# Revit family: SupportArms_Toilet_Nero_MeccaCare_Foldable
name_source: partatom
category: Specialty Equipment
units: mm (PartAtom-declared; Revit-internal decimal feet)

## family parameters
Always vertical = Yes
Cut with Voids When Loaded = Yes
Maintain Annotation Orientation = No
OmniClass Number = 23.25.45.11.25.11
OmniClass Title = Physically Challenged Toilet Arm Supports
Part Type = Normal
Room Calculation Point = No
Round Connector Dimension = Use Diameter
Shared = No
Work Plane-Based = No

## types (6) — shared parameters
Assembly Code = D2010
Default Elevation = 1050 mm
IfcExportAs = IfcRailing
IfcExportType = HANDRAIL
Manufacturer = Nero
ManufacturerOverallDepth = 808 mm  [stored 2.65092 ft]
ManufacturerOverallHeight = 210 mm  [stored 0.688976 ft]
ManufacturerOverallWidth = 101 mm  [stored 0.331365 ft]
ModifiedIssue = 20251009 $
URL = https://nerotapware.com.au
Uniclass2015Code = Pr_25_30_36_34
Uniclass2015Title = Grab rails
Uniclass2015Version = Products v1.35

## per-type parameters (varying)
| type | Description | ManufacturerSpecCode | Material | Model | Type Comments |
| Brushed Nickel (NRCR0007BN) | Mecca Care Foldable Toilet Support Arm Brushed Nickel | NRCR0007BN | Metal_Nickel_Nero_Brushed | NRCR0007BN | Support Arms - Toilet - Foldable - Brushed Nickel |
| Chrome (NRCR0007CH) | Mecca Care Foldable Toilet Support Arm Chrome | NRCR0007CH | Metal_Chrome_Nero | NRCR0007CH | Support Arms - Toilet - Foldable - Chrome |
| Matte Black (NRCR0007MB) | Mecca Care Foldable Toilet Support Arm Matte Black | NRCR0007MB | Metal_MatteBlack_Nero | NRCR0007MB | Support Arms - Toilet - Foldable - Matte Black |
| Brushed Gold (NRCR0007BG) | Mecca Care Foldable Toilet Support Arm Brushed Gold | NRCR0007BG | Metal_Gold_Nero_Brushed | NRCR0007BG | Support Arms - Toilet - Foldable - Brushed Gold |
| Gun Metal (NRCR0007GM) | Mecca Care Foldable Toilet Support Arm Gun Metal | NRCR0007GM | Metal_GunMetal_Nero | NRCR0007GM | Support Arms - Toilet - Foldable - Gun Metal |
| Brushed Bronze (NRCR0007BZ) | Mecca Care Foldable Toilet Support Arm Brushed Bronze | NRCR0007BZ | Metal_Bronze_Nero_Brushed | NRCR0007BZ | Support Arms - Toilet - Foldable - Brushed Bronze |

note: [stored X ft] marks values corroborated as IEEE doubles in the binary element streams (Revit-internal decimal feet)

## geometry (parser evidence)
native form markers: Sweep x2
no freeform markers — native parametric forms only
